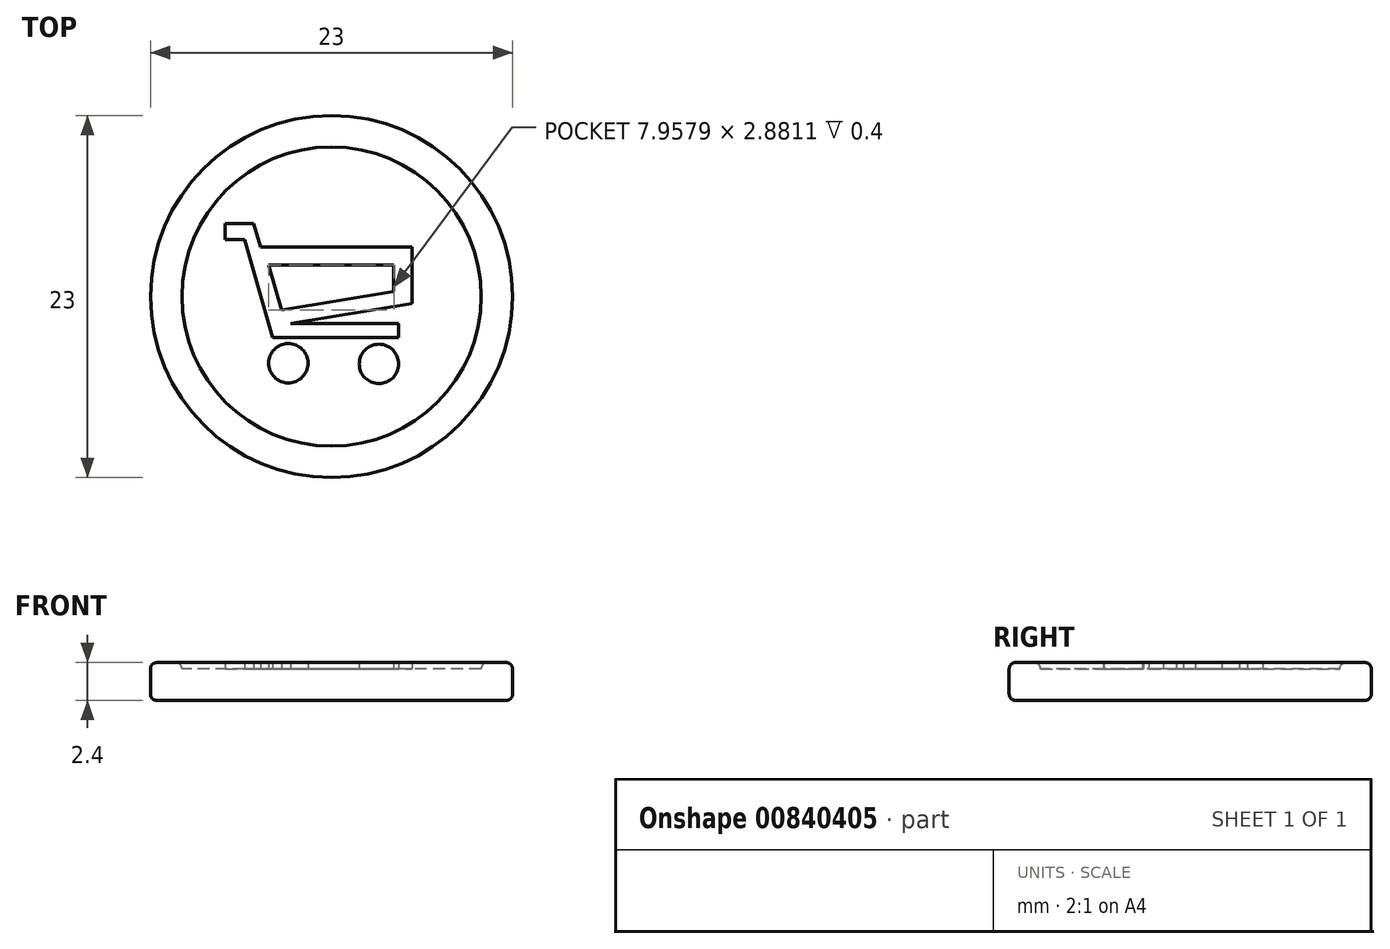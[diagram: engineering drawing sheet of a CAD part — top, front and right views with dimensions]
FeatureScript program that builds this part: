
annotation { "Feature Type Name" : "Feature", "Feature Type Description" : "" }
export const myFeature = defineFeature(function(context is Context, id is Id, definition is map)
    precondition{}
    {
        {
            var Q0;
            Q0=qCreatedBy(makeId("Top.planeOp"),FACE);
            var sketch = newSketch(context, id + "F0", { "sketchPlane" : qUnion([Q0])});
            skCircle(sketch, "E0", {"center": v(0, 0) * mm, "radius": 11.5 * mm});
            skPoint(sketch, "E1.trimOffspring.end.orphan", {"position": v(0.03, -39.26) * mm});
            skPoint(sketch, "E2.center.orphan", {"position": v(0, -33.5) * mm});
            skSolve(sketch);
        }
        {
            var Q0;
            {var subQ0=sQuery(id+"F0.wireOp",EDGE,"E0");var subQ1=makeQuery(id+"F0.imprint","INTERSECT",VERTEX,{"derivedFrom":[subQ0,sQuery(id+"F0.wireOp",EDGE,"17yqRez9-0sNm-4qFj-WzNj-XYPE3Smj19IK")]});Q0=makeQuery(id+"F0.imprint","IMPRINT",FACE,{"disambiguationData":[TD([[makeQuery(id+"F0.imprint","IMPRINT",EDGE,{"disambiguationData":[TD([[subQ1,-1.0]])],"derivedFrom":subQ0}),1.0]])]});}
            var Q1;
            {var subQ1=sQuery(id+"F0.wireOp",EDGE,"17yqRez9-0sNm-4qFj-WzNj-XYPE3Smj19IK");Q1=makeQuery(id+"F0.imprint","IMPRINT",FACE,{"disambiguationData":[TD([[makeQuery(id+"F0.imprint","IMPRINT",EDGE,{"derivedFrom":subQ1}),1.0]])]});}
            extrude(context, id + "F1", {"entities" : qUnion([Q0, Q1]), "depth" : 2 * mm, "offsetDistance" : 25 * mm});
        }
        {
            var Q0;
            Q0=makeQuery(id+"F1.opExtrude","CAP_FACE",FACE,{"disambiguationData":[OSD([sQuery(id+"F0.wireOp",EDGE,"E0"),sQuery(id+"F0.wireOp",EDGE,"17yqRez9-0sNm-4qFj-WzNj-XYPE3Smj19IK"),sQuery(id+"F0.wireOp",EDGE,"st447GzE-i7GB-1to7-X6Aw-wCotyWHXxFLo"),sQuery(id+"F0.wireOp",EDGE,"8Z7i2KwG-6cyb-kCnZ-KfgH-veHT52VF9trH"),sQuery(id+"F0.wireOp",EDGE,"fh5twboJ-bka2-FRvl-eJyA-GtjpmXtnkDHU")])],"isStart":false});
            var sketch = newSketch(context, id + "F2", { "sketchPlane" : qUnion([Q0])});
            skCircle(sketch, "E3", {"center": v(0, 0) * mm, "radius": 11.5 * mm});
            skCircle(sketch, "E4", {"center": v(0, 0) * mm, "radius": 9.5 * mm});
            skSolve(sketch);
        }
        {
            var Q0;
            Q0=makeQuery(id+"F2.imprint","IMPRINT",FACE,{"disambiguationData":[TD([[makeQuery(id+"F2.imprint","IMPRINT",EDGE,{"derivedFrom":sQuery(id+"F2.wireOp",EDGE,"E4")}),-1.0]])]});
            extrude(context, id + "F3", {"entities" : qUnion([Q0]), "operationType" : NewBodyOperationType.ADD, "depth" : .4 * mm, "offsetDistance" : 25 * mm});
        }
        {
            var Q0;
            Q0=makeQuery(id+"F3.boolean.opBoolean","SPLIT",FACE,{"disambiguationData":[TD([makeQuery(id+"F3.opExtrude","SWEPT_FACE",FACE,{"disambiguationData":[OSD([sQuery(id+"F2.wireOp",EDGE,"E4")])]})])],"derivedFrom":makeQuery(id+"F1.opExtrude","CAP_FACE",FACE,{"disambiguationData":[OSD([sQuery(id+"F0.wireOp",EDGE,"E0"),sQuery(id+"F0.wireOp",EDGE,"17yqRez9-0sNm-4qFj-WzNj-XYPE3Smj19IK"),sQuery(id+"F0.wireOp",EDGE,"st447GzE-i7GB-1to7-X6Aw-wCotyWHXxFLo"),sQuery(id+"F0.wireOp",EDGE,"8Z7i2KwG-6cyb-kCnZ-KfgH-veHT52VF9trH")])],"isStart":false})});
            var sketch = newSketch(context, id + "F4", { "sketchPlane" : qUnion([Q0])});
            skLineSegment(sketch, "E5", {"start": v(-6.74, 4.62) * mm, "end": v(-4.95, 4.62) * mm});
            skLineSegment(sketch, "E6", {"start": v(-4.95, 4.62) * mm, "end": v(-4.52, 3.13) * mm});
            skLineSegment(sketch, "E7", {"start": v(-2.6, -1.7) * mm, "end": v(4.26, -1.7) * mm});
            skLineSegment(sketch, "E8", {"start": v(4.26, -1.7) * mm, "end": v(4.26, -2.61) * mm});
            skLineSegment(sketch, "E9", {"start": v(4.26, -2.61) * mm, "end": v(-3.73, -2.61) * mm});
            skLineSegment(sketch, "E10", {"start": v(-3.73, -2.61) * mm, "end": v(-5.53, 3.63) * mm});
            skLineSegment(sketch, "E11", {"start": v(-5.53, 3.63) * mm, "end": v(-6.74, 3.63) * mm});
            skLineSegment(sketch, "E12", {"start": v(-6.74, 3.63) * mm, "end": v(-6.74, 4.62) * mm});
            skLineSegment(sketch, "E13", {"start": v(-4.52, 3.13) * mm, "end": v(5.1, 3.13) * mm});
            skLineSegment(sketch, "E14", {"start": v(5.1, 3.13) * mm, "end": v(5.1, -0.43) * mm});
            skLineSegment(sketch, "E15", {"start": v(5.1, -0.43) * mm, "end": v(-2.6, -1.7) * mm});
            skLineSegment(sketch, "E16", {"start": v(-4, 2.01) * mm, "end": v(3.96, 2.01) * mm});
            skLineSegment(sketch, "E17", {"start": v(3.96, 2.01) * mm, "end": v(3.96, 0.31) * mm});
            skLineSegment(sketch, "E18", {"start": v(-3.17, -0.87) * mm, "end": v(-4, 2.01) * mm});
            skCircle(sketch, "E19", {"center": v(-2.74, -4.23) * mm, "radius": 1.25 * mm});
            skCircle(sketch, "E20", {"center": v(3.01, -4.28) * mm, "radius": 1.25 * mm});
            skLineSegment(sketch, "E21", {"start": v(3.96, 0.31) * mm, "end": v(-3.17, -0.87) * mm});
            skSolve(sketch);
        }
        {
            var Q0;
            Q0=makeQuery(id+"F4.imprint","IMPRINT",FACE,{"disambiguationData":[TD([[makeQuery(id+"F4.imprint","IMPRINT",EDGE,{"derivedFrom":sQuery(id+"F4.wireOp",EDGE,"E5")}),-1.0]])]});
            var Q1;
            Q1=makeQuery(id+"F4.imprint","IMPRINT",FACE,{"disambiguationData":[TD([[makeQuery(id+"F4.imprint","IMPRINT",EDGE,{"derivedFrom":sQuery(id+"F4.wireOp",EDGE,"E19")}),1.0]])]});
            var Q2;
            Q2=makeQuery(id+"F4.imprint","IMPRINT",FACE,{"disambiguationData":[TD([[makeQuery(id+"F4.imprint","IMPRINT",EDGE,{"derivedFrom":sQuery(id+"F4.wireOp",EDGE,"E20")}),1.0]])]});
            extrude(context, id + "F5", {"entities" : qUnion([Q0, Q1, Q2]), "operationType" : NewBodyOperationType.ADD, "depth" : .4 * mm, "offsetDistance" : 25 * mm});
        }
        {
            var Q0;
            Q0=makeQuery(id+"F3.opExtrude","CAP_EDGE",EDGE,{"disambiguationData":[OSD([sQuery(id+"F2.wireOp",EDGE,"E3")])],"isStart":false});
            var Q1;
            Q1=makeQuery(id+"F3.opExtrude","CAP_EDGE",EDGE,{"disambiguationData":[OSD([sQuery(id+"F2.wireOp",EDGE,"E4")])],"isStart":false});
            var Q2;
            Q2=makeQuery(id+"F1.opExtrude","CAP_EDGE",EDGE,{"disambiguationData":[OSD([sQuery(id+"F0.wireOp",EDGE,"E0")])],"isStart":true});
            fillet(context, id + "F6", {"entities" : qUnion([Q0, Q1, Q2]), "radius" : .4 * mm, "tangentPropagation" : true, "allowEdgeOverflow" : false});
        }
    });
